# Revit family: Промышленные откатные ворота с нижней направляющей серии ISG-LG
name_source: partatom
category: Двери
units: mm (PartAtom-declared; Revit-internal decimal feet)

## family parameters
Всегда вертикально = Да
Заголовок OmniClass = Doors
Номер OmniClass = 23.30.10.00
Общий = Нет
Основа = Стена
При загрузке вырезать с полостями = Нет
Точка принадлежности помещению = Нет

## types (1)
- Промышленные откатные ворота с нижней направляющей серии ISG-LG
    --------------------Направляющие-------------------- = --------------------
    --------------------Полотно-------------------- = --------------------
    --------------------Расчет-------------------- = --------------------
    ADSK_URL страницы изделия = https://doorhan.ru
    ADSK_Единица измерения = шт.
    ADSK_Завод-изготовитель = DoorHan
    ADSK_Код изделия = DUS-234-2
    ADSK_Количество = 1
    ADSK_Марка = ISG-LG
    ADSK_Наименование = Промышленные откатные ворота с нижней направляющей серии ISG-LG
    Воздухонепроницаемость по ГОСТ26602.2-99 = 50 Па
    Группа воспламеняемости по ГОСТ 30402-96 = В2 (умеренно горючие). При толщине сэндвич-панели 55 мм
    Группа горючести по ГОСТ 30244-94 = Г2 (умеренно горючие). При толщине сэндвич-панели 55 мм
    Замыкание стены = По основе
    Материал направляющих = DoorHan_Серый
    Материал полотна = DoorHan_Серый
    Материал уплотнения = DoorHan_Черный
    Полотно_Выступ = 30 мм
    Приведенное сопротивление теплопередаче = 0,65м2 *°С/Вт. При толщине сэндвич-панели 55 мм
    Ресурс = 20 000 циклов. Минимальное количество циклов, при котором изготовитель гарантирует отсутствие необходимости в замене какой-либо детали
    Сопротивление ветровой нагрузке = 480 Па
    Функция = Внутренние слои
